# Revit family: Array 7x ACDC Track Spot (NARROW) 4000K
name_source: partatom
category: Lighting Fixtures
units: mm (PartAtom-declared; Revit-internal decimal feet)

## family parameters
Cut with Voids When Loaded = No
Host = Face
Light Source = No
Part Type = Normal
Room Calculation Point = No
Round Connector Dimension = Use Diameter
Shared = No

## types (1)
- Array 7x ACDC Track Spot (NARROW) 4000K
    Beam Angle Degree = 35.5
    Bining = ≤3SDCM
    CCT(K) = 4000
    CRI = 90
    Certification = Available on request
    Colors = White/Black
    Default Elevation = 1219 mm
    Dimmable = Yes
    Driver Type = On-Off/ Dali 2.0/ DT8/BLE/AD
    Driving Current( mA) = 800
    Efficacy (Lm/W) = 91.96
    Efficiency = >92 %
    IP Rating = IP20
    Integrated/Remote = Integrated
    Lamp Flux( lm) = 3257.22
    Lifetime = L80/B10(>50,000hrs@Ta-30Deg C)
    Manufacturer = pluslighttech.
    Rotation = 355.00°
    THD = <10%
    Tilt Angle = 90.00°
    Tuneable = Yes
    UGR = <-6
    URL = https://pluslighttech.com
    Wattage(W) = 35

## geometry (parser evidence)
native form markers: Sweep x26
no freeform markers — native parametric forms only
